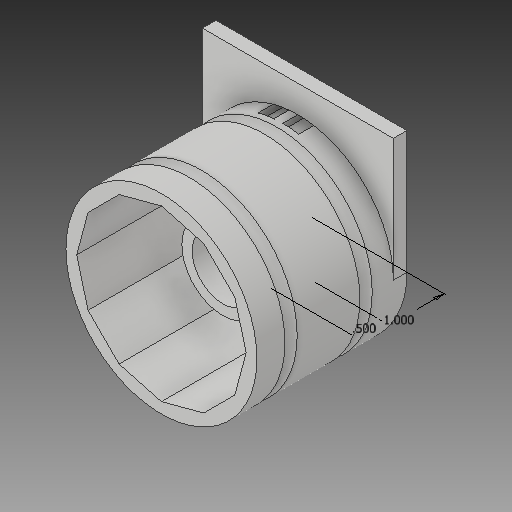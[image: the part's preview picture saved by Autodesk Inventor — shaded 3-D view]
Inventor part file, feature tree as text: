
AUTODESK INVENTOR PART (.ipt)
format: ipt  version: 2018 (Build 220112000, 112)  size: 377,344 bytes
history: native  units: in
note: dims shown in document units (in); Inventor stores cm internally (conversion verified against a paired STEP export)
features: sketch x14, extrude x12, projected_geometry x4, mirror x2, revolve x1
ambient origin geometry x8: Origin, YZ Plane, XZ Plane, XY Plane, X Axis, Y Axis, Z Axis, Center Point
bodies: Solid1 (feature_tree)
feature tree (33):
  extrude  "Extrusion1"  Depth=3.5in
  extrude  "Extrusion2"  Depth=1.75in
  extrude  "Extrusion3"  Depth=0.25in TaperAngle=0.0deg
  extrude  "Extrusion4"  Depth=2.5in TaperAngle=0.0deg
  extrude  "Extrusion6"  Depth=1.5in TaperAngle=0.0deg
  extrude  "Extrusion7"  Depth=1.375in TaperAngle=0.0deg
  revolve  "Revolution1"  [1 undecoded]
  extrude  "Extrusion8"  Depth=3.0in
  extrude  "Extrusion9"  Depth=0.1275in
  sketch  "Sketch11"  dims[d31=0.75in d32=0.625in]
  extrude  "Extrusion10"  Depth=0.75in
  extrude  "Extrusion11"  Depth=0.38in
  extrude  "Extrusion12"  Depth=1.25in
  extrude  "Extrusion13"  Depth=0.75in
  mirror  "Mirror1"
  mirror  "Mirror2"
  sketch  "Sketch1"  dims[d0=3.5in d1=3.5in]
  sketch  "Sketch2"  dims[d2=3.5in d3=1.75in]
  sketch  "Sketch3"  dims[d4=1.75in d5=0.25in d6=0.0in]
  sketch  "Sketch4"  dims[d8=0.0625in d9=2.5in d10=0.0in]
  sketch  "Sketch6"  dims[d11=1.125in d12=1.5in d13=0.0in]
  sketch  "Sketch7"  dims[d14=1.5in d15=1.375in d16=0.0in]
  projected_geometry  "Projected Loop1"
  sketch  "Sketch8"  dims[d21=0.5in d22=1.25in]
  sketch  "Sketch9"  dims[d23=1.0in d24=0.0in d25=3.0in]
  projected_geometry  "Projected Loop2"
  sketch  "Sketch10"  dims[d26=1.0in d27=0.0in d28=0.1275in]
  projected_geometry  "Projected Loop3"
  sketch  "Sketch12"  dims[d33=90.0deg d35=0.38in]
  projected_geometry  "Projected Loop4"
  sketch  "Sketch13"  dims[d36=1.25in d37=1.25in]
  sketch  "Sketch14"  dims[d38=1.0in d39=0.0in d40=0.75in]
  sketch  "Sketch15"  dims[d41=0.125in d42=0.0in d43=1.0in d44=0.5in d45=0.0675in d46=3.5in d47=0.5in d48=0.0in d53=0.2953in d54=0.1181in d55=0.1181in d56=0.2953in d57=14.1732in d59=360.0deg d61=15.0deg d62=0.5256in d63=0.0in d64=0.2135in d69=1.0in d70=0.0in d71=1.25in d72=1.25in d73=1.25in d74=1.25in d75=2.0in d76=1.0in d77=0.3051in d78=0.6102in d79=0.0791in d80=1.0in d81=0.0in]
note: 1 required parameter value undecoded (feature->parameter linkage not recoverable at this tier; creation-order binding heuristic only, values carry confidence <= 0.55)
